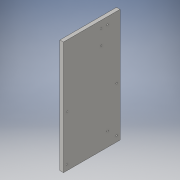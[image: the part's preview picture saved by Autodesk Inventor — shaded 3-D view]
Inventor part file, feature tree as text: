
AUTODESK INVENTOR PART (.ipt)
format: ipt  version: 2016 (Build 200138000, 138)  size: 120,320 bytes
history: native  units: in
note: dims shown in document units (in); Inventor stores cm internally (conversion verified against a paired STEP export)
features: sketch x4, hole x3, extrude x1
ambient origin geometry x8: Origin, YZ Plane, XZ Plane, XY Plane, X Axis, Y Axis, Z Axis, Center Point
bodies: Solid1 (feature_tree)
feature tree (8):
  extrude  "Extrusion1"  Depth=4.0in
  hole  "Hole1"  [1 undecoded]
  hole  "Hole2"  [1 undecoded]
  hole  "Hole3"  [1 undecoded]
  sketch  "Sketch1"  dims[d0=8.0in d1=4.0in]
  sketch  "Sketch2"  dims[d2=0.25in d3=0.0in d4=1.0in]
  sketch  "Sketch3"  dims[d5=3.11in d6=0.5in]
  sketch  "Sketch4"  dims[d7=3.11in d8=0.1024in d9=0.75in d10=0.375in d11=0.25in d12=0.5635in d13=1.0in d14=0.8108in d15=0.3937in d16=0.3937in d17=0.25in d18=0.25in d19=3.6063in d20=0.25in d21=0.25in d22=3.6063in d23=0.1024in d24=0.75in d25=0.375in d26=0.25in d27=0.5635in d28=1.0in d29=0.8108in d30=0.5in d32=1.061in d34=0.1094in d35=0.75in d36=0.375in d37=0.25in d38=0.5635in d39=1.0in d40=0.8108in d41=2.652in d42=2.652in]
note: 3 required parameter values undecoded (feature->parameter linkage not recoverable at this tier; creation-order binding heuristic only, values carry confidence <= 0.55)
